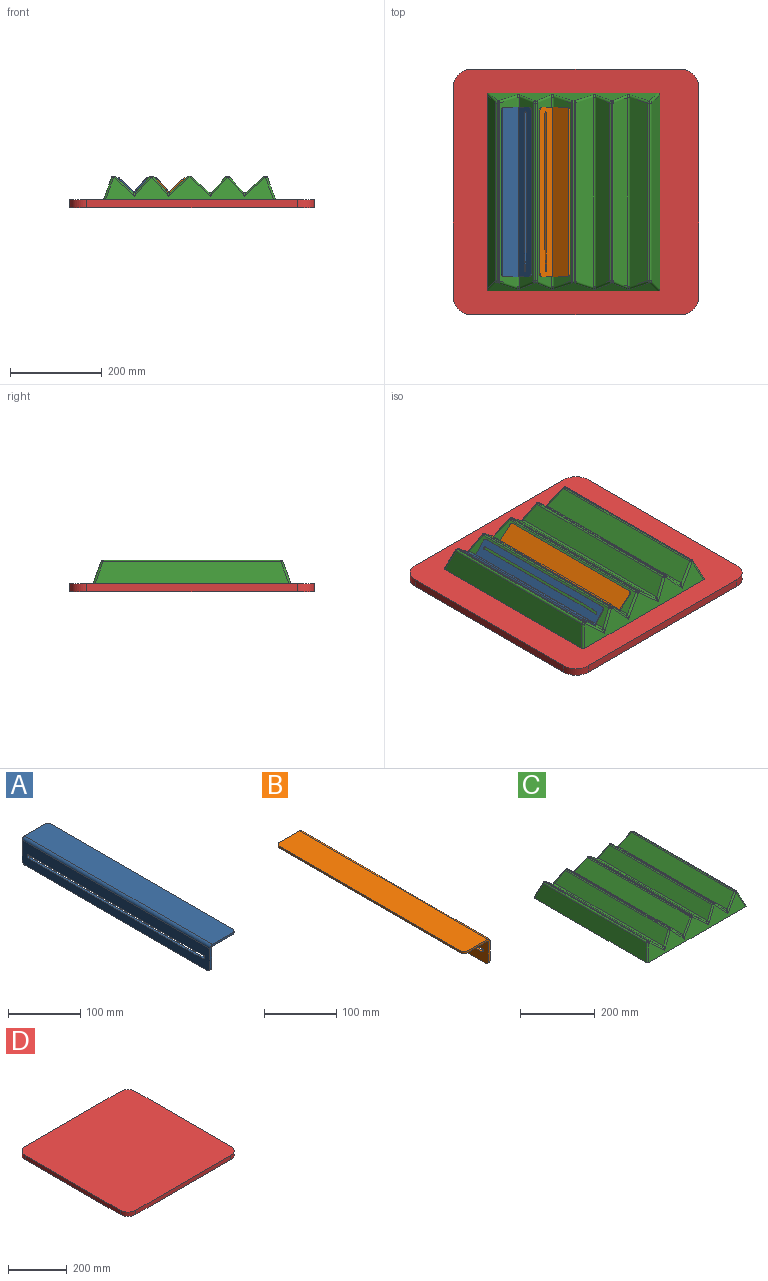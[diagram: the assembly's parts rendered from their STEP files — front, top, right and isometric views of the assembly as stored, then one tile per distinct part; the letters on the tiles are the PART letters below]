
ASSEMBLY  parts=4 mates=5
PART A: 20 faces, bbox 50.8x368.3x44.5 mm
  f0: plane 368.3x39.69mm, normal (1,0,0), area 12630.9mm2, adj f2,f6,f7,f8,f10,f11,f12,f13
  f1: plane 368.3x39.69mm, normal (-1,0,0), area 12630.9mm2, adj f2,f6,f7,f9,f10,f11,f12,f13
  f2: plane 355.6x3.18mm, normal (0,0,-1), area 1129mm2, adj f0,f1,f17,f19
  f3: plane 368.3x46.04mm, normal (0,0,1), area 16938.3mm2, adj f4,f6,f7,f9,f16,f18
  f4: plane 355.6x3.18mm, normal (1,0,0), area 1129mm2, adj f3,f5,f16,f18
  f5: plane 368.3x46.04mm, normal (0,0,-1), area 16938.3mm2, adj f4,f6,f7,f8,f16,f18
  f6: plane 44.45x38.1mm, normal (0,-1,0), area 247.7mm2, adj f0,f1,f3,f5,f8,f9,f18,f19
  f7: plane 44.45x38.1mm, normal (0,1,0), area 247.7mm2, adj f0,f1,f3,f5,f8,f9,f16,f17
  f8: cylinder r=1.59mm len=368.3mm, axis (0,1,0), area 918.4mm2, adj f0,f5,f6,f7
  f9: cylinder r=4.76mm len=368.3mm, axis (0,-1,0), area 2755.2mm2, adj f1,f3,f6,f7
  f10: cylinder r=2.83mm len=5.66mm, axis (1,0,0), area 28.3mm2, adj f0,f1,f11,f15
  f11: cylinder r=1019.47mm len=50.94mm, axis (1,0,0), area 161.8mm2, adj f0,f1,f10,f12
  f12: plane 292.1x3.18mm, normal (0,0,1), area 927.4mm2, adj f0,f1,f11,f13
  f13: cylinder r=2.83mm len=5.67mm, axis (1,0,0), area 28.3mm2, adj f0,f1,f12,f14
  f14: plane 292.1x3.18mm, normal (0,0,-1), area 927.4mm2, adj f0,f1,f13,f15
  f15: cylinder r=1013.8mm len=50.66mm, axis (1,0,0), area 160.9mm2, adj f0,f1,f10,f14
  f16: cylinder r=6.35mm len=6.35mm, axis (0,0,1), area 31.7mm2, adj f3,f4,f5,f7
  f17: cylinder r=6.35mm len=6.35mm, axis (1,0,0), area 31.7mm2, adj f0,f1,f2,f7
  f18: cylinder r=6.35mm len=6.35mm, axis (0,0,-1), area 31.7mm2, adj f3,f4,f5,f6
  f19: cylinder r=6.35mm len=6.35mm, axis (-1,0,0), area 31.7mm2, adj f0,f1,f2,f6
PART B: 20 faces, bbox 50.8x368.3x44.5 mm
  f0: plane 368.3x39.69mm, normal (1,0,0), area 12630.9mm2, adj f3,f6,f7,f9,f10,f11,f12,f13
  f1: plane 368.3x39.69mm, normal (-1,0,0), area 12630.9mm2, adj f3,f6,f7,f8,f10,f11,f12,f13
  f2: plane 368.3x46.04mm, normal (0,0,1), area 16938.3mm2, adj f5,f6,f7,f9,f17,f19
  f3: plane 355.6x3.18mm, normal (0,0,-1), area 1129mm2, adj f0,f1,f16,f18
  f4: plane 368.3x46.04mm, normal (0,0,-1), area 16938.3mm2, adj f5,f6,f7,f8,f17,f19
  f5: plane 355.6x3.18mm, normal (-1,0,0), area 1129mm2, adj f2,f4,f17,f19
  f6: plane 44.45x38.1mm, normal (0,-1,0), area 247.7mm2, adj f0,f1,f2,f4,f8,f9,f18,f19
  f7: plane 44.45x38.1mm, normal (0,1,0), area 247.7mm2, adj f0,f1,f2,f4,f8,f9,f16,f17
  f8: cylinder r=1.59mm len=368.3mm, axis (0,1,0), area 918.4mm2, adj f1,f4,f6,f7
  f9: cylinder r=4.76mm len=368.3mm, axis (0,-1,0), area 2755.2mm2, adj f0,f2,f6,f7
  f10: cylinder r=2.83mm len=5.66mm, axis (1,0,0), area 28.3mm2, adj f0,f1,f11,f15
  f11: cylinder r=1019.47mm len=50.94mm, axis (1,0,0), area 161.8mm2, adj f0,f1,f10,f12
  f12: plane 292.1x3.18mm, normal (0,0,1), area 927.4mm2, adj f0,f1,f11,f13
  f13: cylinder r=2.83mm len=5.67mm, axis (1,0,0), area 28.3mm2, adj f0,f1,f12,f14
  f14: plane 292.1x3.18mm, normal (0,0,-1), area 927.4mm2, adj f0,f1,f13,f15
  f15: cylinder r=1013.8mm len=50.66mm, axis (1,0,0), area 160.9mm2, adj f0,f1,f10,f14
  f16: cylinder r=6.35mm len=6.35mm, axis (1,0,0), area 31.7mm2, adj f0,f1,f3,f7
  f17: cylinder r=6.35mm len=6.35mm, axis (0,0,-1), area 31.7mm2, adj f2,f4,f5,f7
  f18: cylinder r=6.35mm len=6.35mm, axis (-1,0,0), area 31.7mm2, adj f0,f1,f3,f6
  f19: cylinder r=6.35mm len=6.35mm, axis (0,0,1), area 31.7mm2, adj f2,f4,f5,f6
PART C: 98 faces, bbox 375x431.1x51.4 mm
  f0: plane 410.91x32.81mm, normal (-0.75,0,0.66), area 17514.4mm2, adj f61,f67,f70,f95
  f1: plane 411.49x37.8mm, normal (0.66,0,0.75), area 20193.3mm2, adj f71,f74,f77,f94,f95,f96
  f2: plane 387.03x1.2mm, normal (0,0,1), area 466.2mm2, adj f64,f72,f73,f77
  f3: plane 421.73x47.67mm, normal (-0.94,0,0.34), area 20512.4mm2, adj f4,f63,f64,f65
  f4: plane 430.68x374.59mm, normal (0,0,-1), area 161309.8mm2, adj f3,f5,f16,f17,f18,f19,f63,f65
  f5: plane 421.73x47.67mm, normal (0.94,0,0.34), area 20512.4mm2, adj f4,f18,f19,f20
  f6: plane 387.03x1.2mm, normal (0,0,1), area 466.2mm2, adj f20,f23,f24,f25
  f7: plane 411.49x37.8mm, normal (-0.66,0,0.75), area 20193.3mm2, adj f25,f28,f29,f89,f90,f91
  f8: plane 410.91x32.81mm, normal (0.75,0,0.66), area 17514.4mm2, adj f30,f31,f32,f90
  f9: plane 387.03x2.07mm, normal (0,0,1), area 802.2mm2, adj f32,f35,f36,f37
  f10: plane 410.91x32.81mm, normal (-0.75,0,0.66), area 17514.4mm2, adj f37,f40,f41,f85
  f11: plane 411.49x37.8mm, normal (0.66,0,0.75), area 20193.3mm2, adj f42,f43,f44,f84,f85,f86
  f12: plane 387.03x2.73mm, normal (0,0,1), area 1056.1mm2, adj f44,f47,f48,f49
  f13: plane 411.49x37.8mm, normal (-0.66,0,0.75), area 20193.3mm2, adj f49,f52,f53,f79,f80,f81
  f14: plane 410.91x32.81mm, normal (0.75,0,0.66), area 17514.4mm2, adj f54,f55,f56,f80
  f15: plane 387.03x2.07mm, normal (0,0,1), area 802.2mm2, adj f56,f59,f60,f61
  f16: plane 365.64x47.67mm, normal (0,-0.94,0.34), area 10833.1mm2, adj f4,f18,f23,f28,f30,f35,f40,f42
  f17: plane 365.64x47.67mm, normal (0,0.94,0.34), area 10833.1mm2, adj f4,f19,f24,f29,f31,f36,f41,f43
  f18: cylinder r=4.76mm len=48.77mm, axis (0.32,-0.32,-0.89), area 374mm2, adj f4,f5,f16,f21
  f19: cylinder r=4.76mm len=48.77mm, axis (0.32,0.32,-0.89), area 374mm2, adj f4,f5,f17,f22
  f20: cylinder r=4.76mm len=387.03mm, axis (0,1,0), area 2251.9mm2, adj f5,f6,f21,f22
  f21: sphere r=4.76mm, area 20.7mm2, adj f18,f20,f23
  f22: sphere r=4.76mm, area 20.7mm2, adj f19,f20,f24
  f23: cylinder r=4.76mm len=4.48mm, axis (1,0,0), area 7mm2, adj f6,f16,f21,f26
  f24: cylinder r=4.76mm len=4.48mm, axis (1,0,0), area 7mm2, adj f6,f17,f22,f27
  f25: cylinder r=4.76mm len=387.03mm, axis (0,1,0), area 1339.4mm2, adj f6,f7,f26,f27
  f26: sphere r=4.76mm, area 11.8mm2, adj f23,f25,f28
  f27: sphere r=4.76mm, area 11.8mm2, adj f24,f25,f29
  f28: cylinder r=4.76mm len=48.08mm, axis (0.73,0.24,0.65), area 350.5mm2, adj f7,f16,f26,f92
  f29: cylinder r=4.76mm len=48.08mm, axis (0.73,-0.24,0.65), area 350.5mm2, adj f7,f17,f27,f88
  f30: cylinder r=4.76mm len=41.6mm, axis (0.64,-0.26,-0.72), area 316.5mm2, adj f8,f16,f33,f91,f92
  f31: cylinder r=4.76mm len=41.6mm, axis (0.64,0.26,-0.72), area 316.5mm2, adj f8,f17,f34,f88,f89
  f32: cylinder r=4.76mm len=387.03mm, axis (0,1,0), area 1556mm2, adj f8,f9,f33,f34
  f33: sphere r=4.76mm, area 13.8mm2, adj f30,f32,f35
  f34: sphere r=4.76mm, area 13.8mm2, adj f31,f32,f36
  f35: cylinder r=4.76mm len=4.48mm, axis (1,0,0), area 12.1mm2, adj f9,f16,f33,f38
  f36: cylinder r=4.76mm len=4.48mm, axis (1,0,0), area 12.1mm2, adj f9,f17,f34,f39
  f37: cylinder r=4.76mm len=387.03mm, axis (0,-1,0), area 1556mm2, adj f9,f10,f38,f39
  f38: sphere r=4.76mm, area 13.8mm2, adj f35,f37,f40
  f39: sphere r=4.76mm, area 13.8mm2, adj f36,f37,f41
  f40: cylinder r=4.76mm len=41.6mm, axis (0.64,0.26,0.72), area 316.5mm2, adj f10,f16,f38,f86,f87
  f41: cylinder r=4.76mm len=41.6mm, axis (0.64,-0.26,0.72), area 316.5mm2, adj f10,f17,f39,f83,f84
  f42: cylinder r=4.76mm len=48.08mm, axis (0.73,-0.24,-0.65), area 350.5mm2, adj f11,f16,f45,f87
  f43: cylinder r=4.76mm len=48.08mm, axis (0.73,0.24,-0.65), area 350.5mm2, adj f11,f17,f46,f83
  f44: cylinder r=4.76mm len=387.03mm, axis (0,-1,0), area 1339.4mm2, adj f11,f12,f45,f46
  f45: sphere r=4.76mm, area 11.8mm2, adj f42,f44,f47
  f46: sphere r=4.76mm, area 11.8mm2, adj f43,f44,f48
  f47: cylinder r=4.76mm len=4.48mm, axis (1,0,0), area 15.9mm2, adj f12,f16,f45,f50
  f48: cylinder r=4.76mm len=4.48mm, axis (1,0,0), area 15.9mm2, adj f12,f17,f46,f51
  f49: cylinder r=4.76mm len=387.03mm, axis (0,1,0), area 1339.4mm2, adj f12,f13,f50,f51
  f50: sphere r=4.76mm, area 11.8mm2, adj f47,f49,f52
  f51: sphere r=4.76mm, area 11.8mm2, adj f48,f49,f53
  f52: cylinder r=4.76mm len=48.08mm, axis (0.73,0.24,0.65), area 350.5mm2, adj f13,f16,f50,f82
  f53: cylinder r=4.76mm len=48.08mm, axis (0.73,-0.24,0.65), area 350.5mm2, adj f13,f17,f51,f78
  f54: cylinder r=4.76mm len=41.6mm, axis (0.64,-0.26,-0.72), area 316.5mm2, adj f14,f16,f57,f81,f82
  f55: cylinder r=4.76mm len=41.6mm, axis (0.64,0.26,-0.72), area 316.5mm2, adj f14,f17,f58,f78,f79
  f56: cylinder r=4.76mm len=387.03mm, axis (0,-1,0), area 1556mm2, adj f14,f15,f57,f58
  f57: sphere r=4.76mm, area 13.8mm2, adj f54,f56,f59
  f58: sphere r=4.76mm, area 13.8mm2, adj f55,f56,f60
  f59: cylinder r=4.76mm len=4.48mm, axis (1,0,0), area 12.1mm2, adj f15,f16,f57,f62
  f60: cylinder r=4.76mm len=4.48mm, axis (1,0,0), area 12.1mm2, adj f15,f17,f58,f66
  f61: cylinder r=4.76mm len=387.03mm, axis (0,-1,0), area 1556mm2, adj f0,f15,f62,f66
  f62: sphere r=4.76mm, area 13.8mm2, adj f59,f61,f67
  f63: cylinder r=4.76mm len=48.77mm, axis (0.32,0.32,0.89), area 374mm2, adj f3,f4,f16,f68
  f64: cylinder r=4.76mm len=387.03mm, axis (0,1,0), area 2251.9mm2, adj f2,f3,f68,f69
  f65: cylinder r=4.76mm len=48.77mm, axis (0.32,-0.32,0.89), area 374mm2, adj f3,f4,f17,f69
  f66: sphere r=4.76mm, area 13.8mm2, adj f60,f61,f70
  f67: cylinder r=4.76mm len=41.6mm, axis (0.64,0.26,0.72), area 316.5mm2, adj f0,f16,f62,f96,f97
  f68: sphere r=4.76mm, area 20.7mm2, adj f63,f64,f72
  f69: sphere r=4.76mm, area 20.7mm2, adj f64,f65,f73
  f70: cylinder r=4.76mm len=41.6mm, axis (0.64,-0.26,0.72), area 316.5mm2, adj f0,f17,f66,f93,f94
  f71: cylinder r=4.76mm len=48.08mm, axis (0.73,-0.24,-0.65), area 350.5mm2, adj f1,f16,f75,f97
  f72: cylinder r=4.76mm len=4.48mm, axis (1,0,0), area 7mm2, adj f2,f16,f68,f75
  f73: cylinder r=4.76mm len=4.48mm, axis (1,0,0), area 7mm2, adj f2,f17,f69,f76
  f74: cylinder r=4.76mm len=48.08mm, axis (0.73,0.24,-0.65), area 350.5mm2, adj f1,f17,f76,f93
  f75: sphere r=4.76mm, area 11.8mm2, adj f71,f72,f77
  f76: sphere r=4.76mm, area 11.8mm2, adj f73,f74,f77
  f77: cylinder r=4.76mm len=387.03mm, axis (0,1,0), area 1339.4mm2, adj f1,f2,f75,f76
  f78: bspline ~8.63x6.91mm, area 38.3mm2, adj f53,f55,f79
  f79: bspline ~6.72x1.57mm, area 1.5mm2, adj f13,f55,f78,f80
  f80: cylinder r=4.76mm len=410.91mm, axis (0,-1,0), area 3074mm2, adj f13,f14,f79,f81
  f81: bspline ~6.72x1.57mm, area 1.5mm2, adj f13,f54,f80,f82
  f82: bspline ~8.63x6.91mm, area 38.3mm2, adj f52,f54,f81
  f83: bspline ~8.63x6.91mm, area 38.3mm2, adj f41,f43,f84
  f84: bspline ~6.92x3.86mm, area 1.5mm2, adj f11,f41,f83,f85
  f85: cylinder r=4.76mm len=410.91mm, axis (0,-1,0), area 3074mm2, adj f10,f11,f84,f86
  f86: bspline ~6.92x3.86mm, area 1.5mm2, adj f11,f40,f85,f87
  f87: bspline ~8.63x6.91mm, area 38.3mm2, adj f40,f42,f86
  f88: bspline ~8.63x6.91mm, area 38.3mm2, adj f29,f31,f89
  f89: bspline ~6.92x3.86mm, area 1.5mm2, adj f7,f31,f88,f90
  f90: cylinder r=4.76mm len=410.91mm, axis (0,-1,0), area 3074mm2, adj f7,f8,f89,f91
  f91: bspline ~6.92x3.86mm, area 1.5mm2, adj f7,f30,f90,f92
  f92: bspline ~8.63x6.91mm, area 38.3mm2, adj f28,f30,f91
  f93: bspline ~8.63x6.91mm, area 38.3mm2, adj f70,f74,f94
  f94: bspline ~6.72x1.57mm, area 1.5mm2, adj f1,f70,f93,f95
  f95: cylinder r=4.76mm len=410.91mm, axis (0,1,0), area 3074mm2, adj f0,f1,f94,f96
  f96: bspline ~6.72x1.57mm, area 1.5mm2, adj f1,f67,f95,f97
  f97: bspline ~8.68x7.4mm, area 38.4mm2, adj f67,f71,f96
PART D: 10 faces, bbox 533.4x533.4x17.8 mm
  f0: plane 457.2x17.78mm, normal (1,0,0), area 8129mm2, adj f1,f7,f8,f9
  f1: cylinder r=38.1mm len=38.1mm, axis (0,0,-1), area 1064.1mm2, adj f0,f2,f8,f9
  f2: plane 457.2x17.78mm, normal (0,1,0), area 8129mm2, adj f1,f3,f8,f9
  f3: cylinder r=38.1mm len=38.1mm, axis (0,0,-1), area 1064.1mm2, adj f2,f4,f8,f9
  f4: plane 457.2x17.78mm, normal (-1,0,0), area 8129mm2, adj f3,f5,f8,f9
  f5: cylinder r=38.1mm len=38.1mm, axis (0,0,-1), area 1064.1mm2, adj f4,f6,f8,f9
  f6: plane 457.2x17.78mm, normal (0,-1,0), area 8129mm2, adj f5,f7,f8,f9
  f7: cylinder r=38.1mm len=38.1mm, axis (0,0,-1), area 1064.1mm2, adj f0,f6,f8,f9
  f8: plane 533.4x533.4mm, normal (0,0,1), area 283269.5mm2, adj f0,f1,f2,f3,f4,f5,f6,f7
  f9: plane 533.4x533.4mm, normal (0,0,-1), area 283269.5mm2, adj f0,f1,f2,f3,f4,f5,f6,f7
PLACE A rot(axis=(0,-1,0),138.4deg) t=(-137.42,-333.38,213.17)mm
PLACE B rot(axis=(0,1,0),138.4deg) t=(-74.98,-333.38,-293.07)mm
PLACE C t=(141.64,463.55,12.7)mm
PLACE D t=(0,0,-17.91)mm
MATE planar A.f1 <-> C.f0  axis (0.75,0,-0.66) through (157.78,266.7,30.85)mm
MATE planar A.f3 <-> C.f1  axis (-0.66,0,-0.75) through (120.89,266.7,31.14)mm
MATE planar B.f2 <-> C.f13  axis (0.66,0,-0.75) through (236.24,266.7,31.14)mm
MATE planar B.f0 <-> C.f14  axis (-0.75,0,-0.66) through (199.35,266.7,30.85)mm
MATE planar C.f4 <-> D.f8  axis (0,0,-1) through (261.38,266.7,-0.13)mm
